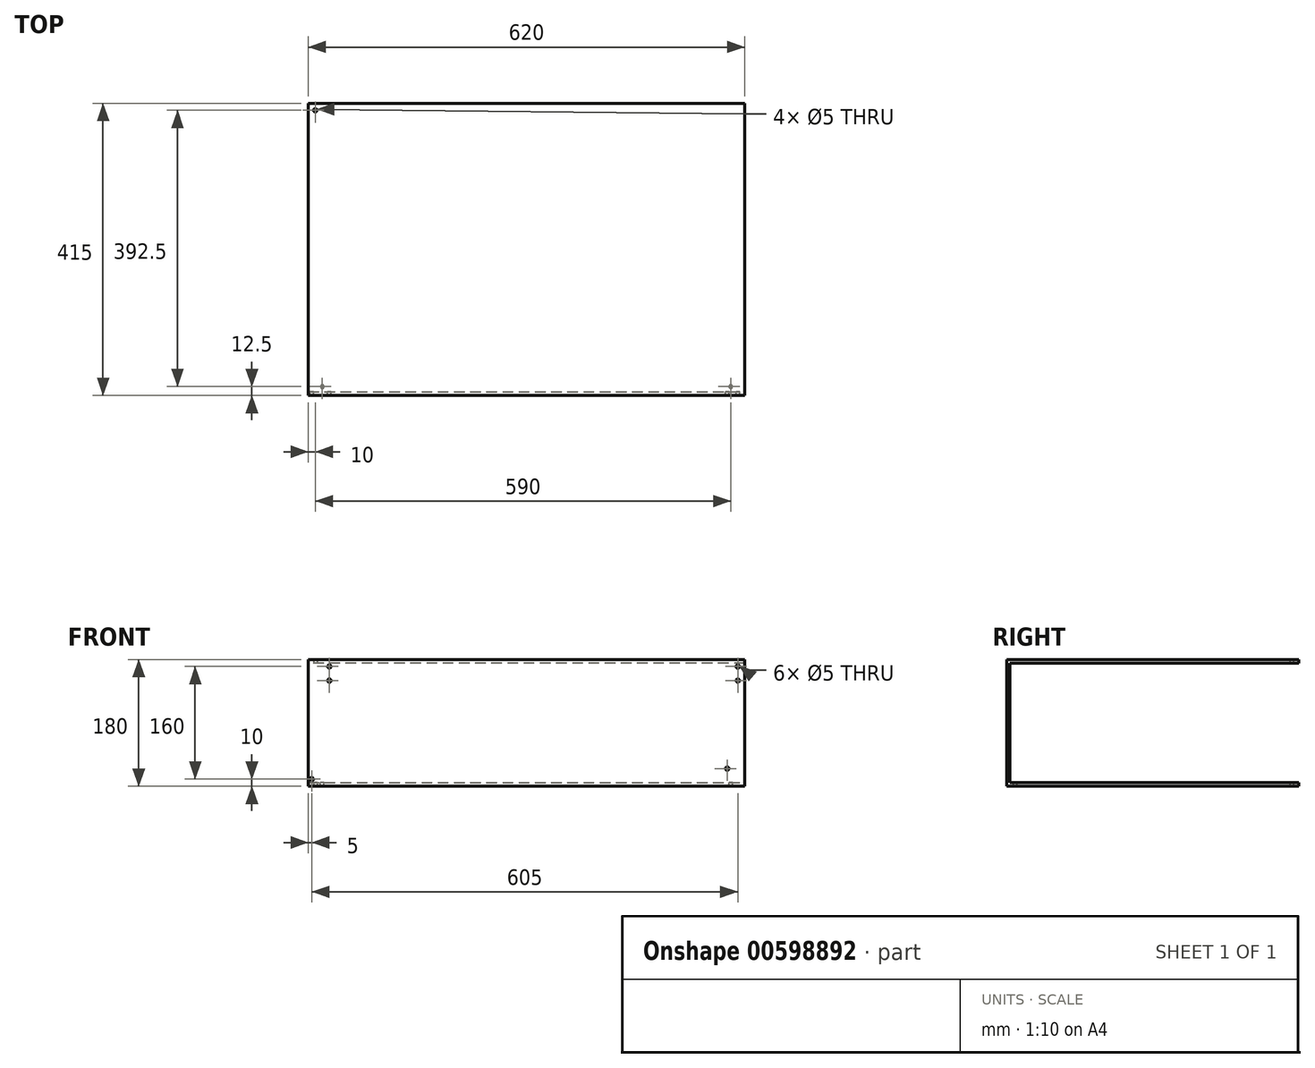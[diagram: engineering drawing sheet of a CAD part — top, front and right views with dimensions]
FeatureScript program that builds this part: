
annotation { "Feature Type Name" : "Feature", "Feature Type Description" : "" }
export const myFeature = defineFeature(function(context is Context, id is Id, definition is map)
    precondition{}
    {
        {
            var Q0;
            Q0=qCreatedBy(makeId("Top.planeOp"),FACE);
            var sketch = newSketch(context, id + "F0", { "sketchPlane" : qUnion([Q0])});
            skLineSegment(sketch, "E0.bottom", {"start": v(310, -207.5) * mm, "end": v(-310, -207.5) * mm});
            skLineSegment(sketch, "E0.top", {"start": v(310, 207.5) * mm, "end": v(-310, 207.5) * mm});
            skLineSegment(sketch, "E0.left", {"start": v(310, -207.5) * mm, "end": v(310, 207.5) * mm});
            skLineSegment(sketch, "E0.right", {"start": v(-310, -207.5) * mm, "end": v(-310, 207.5) * mm});
            skPoint(sketch, "E0.middle", {"position": v(0, 0) * mm});
            skSolve(sketch);
        }
        {
            var Q0;
            Q0=qSketchRegion(id+"F0",true);
            extrude(context, id + "F1", {"entities" : qUnion([Q0]), "depth" : 5 * mm, "offsetDistance" : 25 * mm});
        }
        {
            var Q0;
            Q0=makeQuery(id+"F1.opExtrude","CAP_FACE",FACE,{"disambiguationData":[OSD([sQuery(id+"F0.wireOp",EDGE,"E0.bottom"),sQuery(id+"F0.wireOp",EDGE,"E0.top"),sQuery(id+"F0.wireOp",EDGE,"E0.left"),sQuery(id+"F0.wireOp",EDGE,"E0.right")])],"isStart":false});
            var sketch = newSketch(context, id + "F2", { "sketchPlane" : qUnion([Q0])});
            skLineSegment(sketch, "E1", {"start": v(-310, -202.5) * mm, "end": v(310, -202.5) * mm});
            skLineSegment(sketch, "E2", {"start": v(310, -202.5) * mm, "end": v(310, -207.5) * mm});
            skLineSegment(sketch, "E3", {"start": v(310, -207.5) * mm, "end": v(-310, -207.5) * mm});
            skLineSegment(sketch, "E4", {"start": v(-310, -207.5) * mm, "end": v(-310, -202.5) * mm});
            skSolve(sketch);
        }
        {
            var Q0;
            Q0=makeQuery(id+"F2.imprint","IMPRINT",FACE,{"disambiguationData":[TD([[makeQuery(id+"F2.imprint","IMPRINT",EDGE,{"derivedFrom":sQuery(id+"F2.wireOp",EDGE,"E1")}),-1.0]])]});
            extrude(context, id + "F3", {"entities" : qUnion([Q0]), "operationType" : NewBodyOperationType.ADD, "depth" : 175 * mm, "offsetDistance" : 25 * mm});
        }
        {
            var Q0;
            Q0=makeQuery(id+"F3.boolean.opBoolean","MERGE",FACE,{"derivedFrom":[makeQuery(id+"F1.opExtrude","SWEPT_FACE",FACE,{"disambiguationData":[OSD([sQuery(id+"F0.wireOp",EDGE,"E0.bottom")])]}),makeQuery(id+"F3.opExtrude","SWEPT_FACE",FACE,{"disambiguationData":[OSD([sQuery(id+"F2.wireOp",EDGE,"E3")])]})]});
            var sketch = newSketch(context, id + "F4", { "sketchPlane" : qUnion([Q0])});
            skLineSegment(sketch, "E5", {"start": v(300, 180) * mm, "end": v(300, 138.82) * mm, "construction": true});
            skPoint(sketch, "E6", {"position": v(300, 170) * mm});
            skPoint(sketch, "E7", {"position": v(300, 150) * mm});
            skSolve(sketch);
        }
        {
            var Q0;
            Q0=sQuery(id+"F4.wireOp",VERTEX,"E6");
            var Q1;
            Q1=makeQuery(id+"F1.opExtrude","SWEPT_BODY",BODY,{"disambiguationData":[OSD([sQuery(id+"F0.wireOp",EDGE,"E0.bottom"),sQuery(id+"F0.wireOp",EDGE,"E0.top"),sQuery(id+"F0.wireOp",EDGE,"E0.left"),sQuery(id+"F0.wireOp",EDGE,"E0.right")])]});
            hole(context, id + "F5", {"style" : HoleStyle.SIMPLE, "endStyle" : HoleEndStyle.THROUGH, "holeDiameter" : 5 * mm, "majorDiameter" : 5 * mm, "isTappedThrough" : true, "tappedDepth" : 12 * mm, "tapClearance" : 3, "locations" : qUnion([Q0]), "scope" : qUnion([Q1])});
        }
        {
            var Q0;
            Q0=makeQuery(id+"F3.boolean.opBoolean","MERGE",FACE,{"derivedFrom":[makeQuery(id+"F1.opExtrude","SWEPT_FACE",FACE,{"disambiguationData":[OSD([sQuery(id+"F0.wireOp",EDGE,"E0.bottom")])]}),makeQuery(id+"F3.opExtrude","SWEPT_FACE",FACE,{"disambiguationData":[OSD([sQuery(id+"F2.wireOp",EDGE,"E3")])]})]});
            var sketch = newSketch(context, id + "F6", { "sketchPlane" : qUnion([Q0])});
            skLineSegment(sketch, "E8", {"start": v(300, 180) * mm, "end": v(300, 144.67) * mm, "construction": true});
            skPoint(sketch, "E9", {"position": v(300, 150) * mm});
            skSolve(sketch);
        }
        {
            var Q0;
            Q0=sQuery(id+"F6.wireOp",VERTEX,"E9");
            var Q1;
            Q1=makeQuery(id+"F1.opExtrude","SWEPT_BODY",BODY,{"disambiguationData":[OSD([sQuery(id+"F0.wireOp",EDGE,"E0.bottom"),sQuery(id+"F0.wireOp",EDGE,"E0.top"),sQuery(id+"F0.wireOp",EDGE,"E0.left"),sQuery(id+"F0.wireOp",EDGE,"E0.right")])]});
            hole(context, id + "F7", {"style" : HoleStyle.SIMPLE, "endStyle" : HoleEndStyle.THROUGH, "holeDiameter" : 5 * mm, "majorDiameter" : 5 * mm, "isTappedThrough" : true, "tappedDepth" : 12 * mm, "tapClearance" : 3, "locations" : qUnion([Q0]), "scope" : qUnion([Q1])});
        }
        {
            var Q0;
            Q0=makeQuery(id+"F3.boolean.opBoolean","MERGE",FACE,{"derivedFrom":[makeQuery(id+"F1.opExtrude","SWEPT_FACE",FACE,{"disambiguationData":[OSD([sQuery(id+"F0.wireOp",EDGE,"E0.bottom")])]}),makeQuery(id+"F3.opExtrude","SWEPT_FACE",FACE,{"disambiguationData":[OSD([sQuery(id+"F2.wireOp",EDGE,"E3")])]})]});
            var sketch = newSketch(context, id + "F8", { "sketchPlane" : qUnion([Q0])});
            skLineSegment(sketch, "E10", {"start": v(-280, 180) * mm, "end": v(-280, 162.68) * mm, "construction": true});
            skPoint(sketch, "E11", {"position": v(-280, 170) * mm});
            skSolve(sketch);
        }
        {
            var Q0;
            Q0=sQuery(id+"F8.wireOp",VERTEX,"E11");
            var Q1;
            Q1=makeQuery(id+"F1.opExtrude","SWEPT_BODY",BODY,{"disambiguationData":[OSD([sQuery(id+"F0.wireOp",EDGE,"E0.bottom"),sQuery(id+"F0.wireOp",EDGE,"E0.top"),sQuery(id+"F0.wireOp",EDGE,"E0.left"),sQuery(id+"F0.wireOp",EDGE,"E0.right")])]});
            hole(context, id + "F9", {"style" : HoleStyle.SIMPLE, "endStyle" : HoleEndStyle.THROUGH, "holeDiameter" : 5 * mm, "majorDiameter" : 5 * mm, "isTappedThrough" : true, "tappedDepth" : 12 * mm, "tapClearance" : 3, "locations" : qUnion([Q0]), "scope" : qUnion([Q1])});
        }
        {
            var Q0;
            Q0=makeQuery(id+"F3.boolean.opBoolean","MERGE",FACE,{"derivedFrom":[makeQuery(id+"F1.opExtrude","SWEPT_FACE",FACE,{"disambiguationData":[OSD([sQuery(id+"F0.wireOp",EDGE,"E0.bottom")])]}),makeQuery(id+"F3.opExtrude","SWEPT_FACE",FACE,{"disambiguationData":[OSD([sQuery(id+"F2.wireOp",EDGE,"E3")])]})]});
            var sketch = newSketch(context, id + "F10", { "sketchPlane" : qUnion([Q0])});
            skLineSegment(sketch, "E12", {"start": v(-280, 180) * mm, "end": v(-280, 135.53) * mm, "construction": true});
            skPoint(sketch, "E13", {"position": v(-280, 150) * mm});
            skSolve(sketch);
        }
        {
            var Q0;
            Q0=sQuery(id+"F10.wireOp",VERTEX,"E13");
            var Q1;
            Q1=makeQuery(id+"F1.opExtrude","SWEPT_BODY",BODY,{"disambiguationData":[OSD([sQuery(id+"F0.wireOp",EDGE,"E0.bottom"),sQuery(id+"F0.wireOp",EDGE,"E0.top"),sQuery(id+"F0.wireOp",EDGE,"E0.left"),sQuery(id+"F0.wireOp",EDGE,"E0.right")])]});
            hole(context, id + "F11", {"style" : HoleStyle.SIMPLE, "endStyle" : HoleEndStyle.THROUGH, "holeDiameter" : 5 * mm, "majorDiameter" : 5 * mm, "isTappedThrough" : true, "tappedDepth" : 12 * mm, "tapClearance" : 3, "locations" : qUnion([Q0]), "scope" : qUnion([Q1])});
        }
        {
            var Q0;
            Q0=makeQuery(id+"F3.boolean.opBoolean","MERGE",FACE,{"derivedFrom":[makeQuery(id+"F1.opExtrude","SWEPT_FACE",FACE,{"disambiguationData":[OSD([sQuery(id+"F0.wireOp",EDGE,"E0.bottom")])]}),makeQuery(id+"F3.opExtrude","SWEPT_FACE",FACE,{"disambiguationData":[OSD([sQuery(id+"F2.wireOp",EDGE,"E3")])]})]});
            var sketch = newSketch(context, id + "F12", { "sketchPlane" : qUnion([Q0])});
            skLineSegment(sketch, "E14", {"start": v(-310, 10) * mm, "end": v(-305, 10) * mm});
            skSolve(sketch);
        }
        {
            var Q0;
            Q0=sQuery(id+"F12.wireOp",VERTEX,"E14.end");
            var Q1;
            Q1=makeQuery(id+"F1.opExtrude","SWEPT_BODY",BODY,{"disambiguationData":[OSD([sQuery(id+"F0.wireOp",EDGE,"E0.bottom"),sQuery(id+"F0.wireOp",EDGE,"E0.top"),sQuery(id+"F0.wireOp",EDGE,"E0.left"),sQuery(id+"F0.wireOp",EDGE,"E0.right")])]});
            hole(context, id + "F13", {"style" : HoleStyle.SIMPLE, "endStyle" : HoleEndStyle.THROUGH, "holeDiameter" : 5 * mm, "majorDiameter" : 5 * mm, "isTappedThrough" : true, "tappedDepth" : 12 * mm, "tapClearance" : 3, "locations" : qUnion([Q0]), "scope" : qUnion([Q1])});
        }
        {
            var Q0;
            Q0=makeQuery(id+"F1.opExtrude","CAP_FACE",FACE,{"disambiguationData":[OSD([sQuery(id+"F0.wireOp",EDGE,"E0.bottom"),sQuery(id+"F0.wireOp",EDGE,"E0.top"),sQuery(id+"F0.wireOp",EDGE,"E0.left"),sQuery(id+"F0.wireOp",EDGE,"E0.right")])],"isStart":true});
            var sketch = newSketch(context, id + "F14", { "sketchPlane" : qUnion([Q0])});
            skLineSegment(sketch, "E15", {"start": v(290, 207.5) * mm, "end": v(290, 195) * mm});
            skSolve(sketch);
        }
        {
            var Q0;
            Q0=sQuery(id+"F14.wireOp",VERTEX,"E15.end");
            var Q1;
            Q1=makeQuery(id+"F1.opExtrude","SWEPT_BODY",BODY,{"disambiguationData":[OSD([sQuery(id+"F0.wireOp",EDGE,"E0.bottom"),sQuery(id+"F0.wireOp",EDGE,"E0.top"),sQuery(id+"F0.wireOp",EDGE,"E0.left"),sQuery(id+"F0.wireOp",EDGE,"E0.right")])]});
            hole(context, id + "F15", {"style" : HoleStyle.SIMPLE, "endStyle" : HoleEndStyle.THROUGH, "holeDiameter" : 5 * mm, "majorDiameter" : 5 * mm, "isTappedThrough" : true, "tappedDepth" : 12 * mm, "tapClearance" : 3, "locations" : qUnion([Q0]), "scope" : qUnion([Q1])});
        }
        {
            var Q0;
            Q0=makeQuery(id+"F1.opExtrude","CAP_FACE",FACE,{"disambiguationData":[OSD([sQuery(id+"F0.wireOp",EDGE,"E0.bottom"),sQuery(id+"F0.wireOp",EDGE,"E0.top"),sQuery(id+"F0.wireOp",EDGE,"E0.left"),sQuery(id+"F0.wireOp",EDGE,"E0.right")])],"isStart":true});
            var sketch = newSketch(context, id + "F16", { "sketchPlane" : qUnion([Q0])});
            skLineSegment(sketch, "E16", {"start": v(-290, 207.5) * mm, "end": v(-290, 195) * mm});
            skSolve(sketch);
        }
        {
            var Q0;
            Q0=sQuery(id+"F16.wireOp",VERTEX,"E16.end");
            var Q1;
            Q1=makeQuery(id+"F1.opExtrude","SWEPT_BODY",BODY,{"disambiguationData":[OSD([sQuery(id+"F0.wireOp",EDGE,"E0.bottom"),sQuery(id+"F0.wireOp",EDGE,"E0.top"),sQuery(id+"F0.wireOp",EDGE,"E0.left"),sQuery(id+"F0.wireOp",EDGE,"E0.right")])]});
            hole(context, id + "F17", {"style" : HoleStyle.SIMPLE, "endStyle" : HoleEndStyle.THROUGH, "holeDiameter" : 5 * mm, "majorDiameter" : 5 * mm, "isTappedThrough" : true, "tappedDepth" : 12 * mm, "tapClearance" : 3, "locations" : qUnion([Q0]), "scope" : qUnion([Q1])});
        }
        {
            var Q0;
            Q0=makeQuery(id+"F3.boolean.opBoolean","MERGE",FACE,{"derivedFrom":[makeQuery(id+"F1.opExtrude","SWEPT_FACE",FACE,{"disambiguationData":[OSD([sQuery(id+"F0.wireOp",EDGE,"E0.bottom")])]}),makeQuery(id+"F3.opExtrude","SWEPT_FACE",FACE,{"disambiguationData":[OSD([sQuery(id+"F2.wireOp",EDGE,"E3")])]})]});
            var sketch = newSketch(context, id + "F18", { "sketchPlane" : qUnion([Q0])});
            skLineSegment(sketch, "E17", {"start": v(285, 0) * mm, "end": v(285, 25) * mm});
            skSolve(sketch);
        }
        {
            var Q0;
            Q0=sQuery(id+"F18.wireOp",VERTEX,"E17.end");
            var Q1;
            Q1=makeQuery(id+"F1.opExtrude","SWEPT_BODY",BODY,{"disambiguationData":[OSD([sQuery(id+"F0.wireOp",EDGE,"E0.bottom"),sQuery(id+"F0.wireOp",EDGE,"E0.top"),sQuery(id+"F0.wireOp",EDGE,"E0.left"),sQuery(id+"F0.wireOp",EDGE,"E0.right")])]});
            hole(context, id + "F19", {"style" : HoleStyle.SIMPLE, "endStyle" : HoleEndStyle.BLIND, "holeDiameter" : 5 * mm, "majorDiameter" : 5 * mm, "holeDepth" : 11 * mm, "isTappedThrough" : true, "tappedDepth" : 12 * mm, "tapClearance" : 3, "locations" : qUnion([Q0]), "scope" : qUnion([Q1])});
        }
        {
            var Q0;
            Q0=makeQuery(id+"F3.opExtrude","SWEPT_FACE",FACE,{"disambiguationData":[OSD([sQuery(id+"F2.wireOp",EDGE,"E1")])]});
            var sketch = newSketch(context, id + "F20", { "sketchPlane" : qUnion([Q0])});
            skLineSegment(sketch, "E18.bottom", {"start": v(-310, 180) * mm, "end": v(310, 180) * mm});
            skLineSegment(sketch, "E18.top", {"start": v(-310, 175) * mm, "end": v(310, 175) * mm});
            skLineSegment(sketch, "E18.left", {"start": v(-310, 180) * mm, "end": v(-310, 175) * mm});
            skLineSegment(sketch, "E18.right", {"start": v(310, 180) * mm, "end": v(310, 175) * mm});
            skSolve(sketch);
        }
        {
            var Q0;
            Q0=makeQuery(id+"F20.imprint","IMPRINT",FACE,{"disambiguationData":[TD([[makeQuery(id+"F20.imprint","IMPRINT",EDGE,{"derivedFrom":sQuery(id+"F20.wireOp",EDGE,"E18.bottom")}),1.0]])]});
            extrude(context, id + "F21", {"entities" : qUnion([Q0]), "operationType" : NewBodyOperationType.ADD, "depth" : 410 * mm, "offsetDistance" : 25 * mm});
        }
        {
            var Q0;
            Q0=makeQuery(id+"F21.boolean.opBoolean","MERGE",FACE,{"derivedFrom":[makeQuery(id+"F3.opExtrude","CAP_FACE",FACE,{"disambiguationData":[OSD([sQuery(id+"F2.wireOp",EDGE,"E1"),sQuery(id+"F2.wireOp",EDGE,"E2"),sQuery(id+"F2.wireOp",EDGE,"E3"),sQuery(id+"F2.wireOp",EDGE,"E4")])],"isStart":false}),makeQuery(id+"F21.opExtrude","SWEPT_FACE",FACE,{"disambiguationData":[OSD([sQuery(id+"F20.wireOp",EDGE,"E18.bottom")])]})]});
            var sketch = newSketch(context, id + "F22", { "sketchPlane" : qUnion([Q0])});
            skPoint(sketch, "E19", {"position": v(-300, 197.5) * mm});
            skSolve(sketch);
        }
        {
            var Q0;
            Q0=sQuery(id+"F22.wireOp",VERTEX,"E19");
            var Q1;
            Q1=makeQuery(id+"F1.opExtrude","SWEPT_BODY",BODY,{"disambiguationData":[OSD([sQuery(id+"F0.wireOp",EDGE,"E0.bottom"),sQuery(id+"F0.wireOp",EDGE,"E0.top"),sQuery(id+"F0.wireOp",EDGE,"E0.left"),sQuery(id+"F0.wireOp",EDGE,"E0.right")])]});
            hole(context, id + "F23", {"style" : HoleStyle.SIMPLE, "endStyle" : HoleEndStyle.THROUGH, "holeDiameter" : 5 * mm, "majorDiameter" : 5 * mm, "isTappedThrough" : true, "tappedDepth" : 12 * mm, "tapClearance" : 3, "locations" : qUnion([Q0]), "scope" : qUnion([Q1])});
        }
    });
